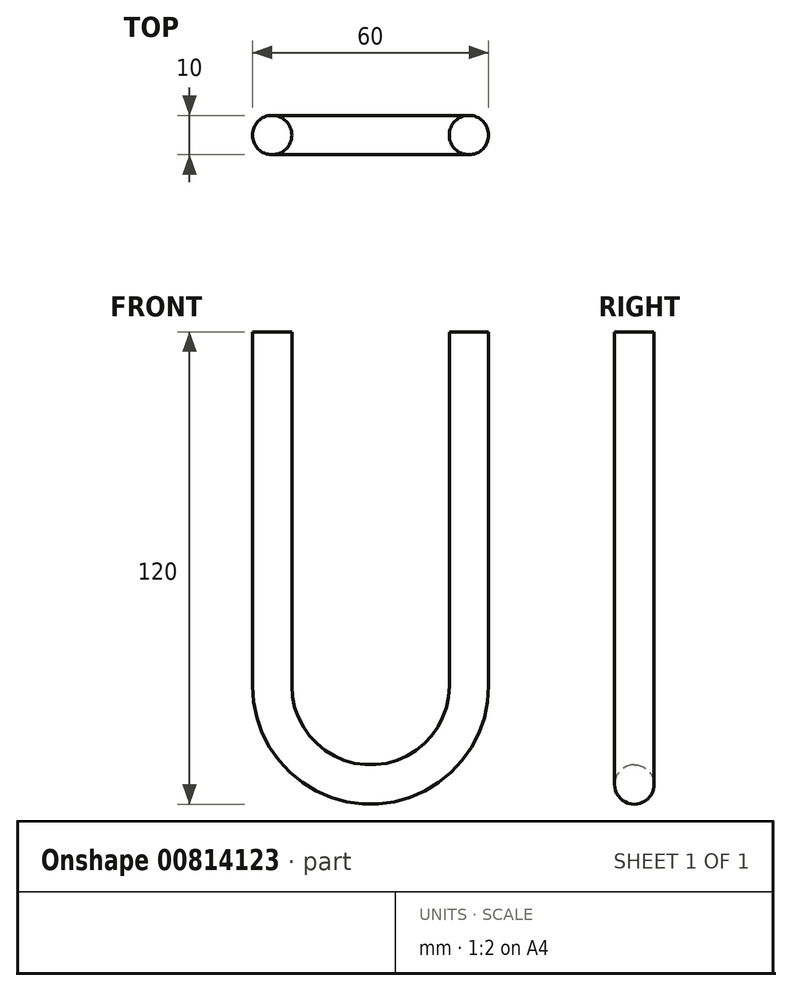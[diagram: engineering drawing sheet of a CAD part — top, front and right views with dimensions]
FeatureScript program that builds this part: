
annotation { "Feature Type Name" : "Feature", "Feature Type Description" : "" }
export const myFeature = defineFeature(function(context is Context, id is Id, definition is map)
    precondition{}
    {
        {
            var Q0;
            Q0=qCreatedBy(makeId("Front.planeOp"),FACE);
            var sketch = newSketch(context, id + "F0", { "sketchPlane" : qUnion([Q0])});
            skLineSegment(sketch, "E0", {"start": v(0, 44.29) * mm, "end": v(0, -45.71) * mm});
            skLineSegment(sketch, "E1", {"start": v(50, 44.29) * mm, "end": v(50, -45.71) * mm});
            skArc(sketch, "E2", {"start": v(0, -45.71) * mm, "mid": v(25, -70.71) * mm, "end": v(50, -45.71) * mm});
            skSolve(sketch);
        }
        {
            var Q0;
            Q0=sQuery(id+"F0.wireOp",EDGE,"E0");
            var Q1;
            Q1=sQuery(id+"F0.wireOp",VERTEX,"E0.start");
            cPlane(context, id + "F1", {"entities" : qUnion([Q0, Q1]), "cplaneType" : CPlaneType.CURVE_POINT, "offset" : 25 * mm, "width" : 150 * mm, "height" : 150 * mm});
        }
        {
            var Q0;
            Q0=qCreatedBy(id+"F1.planeOp",FACE);
            var sketch = newSketch(context, id + "F2", { "sketchPlane" : qUnion([Q0])});
            skCircle(sketch, "E3", {"center": v(50, 0) * mm, "radius": 5 * mm});
            skSolve(sketch);
        }
        {
            var Q0;
            Q0=makeQuery(id+"F2.imprint","IMPRINT",FACE,{"disambiguationData":[TD([[makeQuery(id+"F2.imprint","IMPRINT",EDGE,{"derivedFrom":sQuery(id+"F2.wireOp",EDGE,"E3")}),1.0]])]});
            var Q1;
            Q1=sQuery(id+"F0.wireOp",EDGE,"E1");
            var Q2;
            Q2=sQuery(id+"F0.wireOp",EDGE,"E2");
            var Q3;
            Q3=sQuery(id+"F0.wireOp",EDGE,"E0");
            sweep(context, id + "F3", {"profiles" : qUnion([Q0]), "path" : qUnion([Q1, Q2, Q3])});
        }
    });
